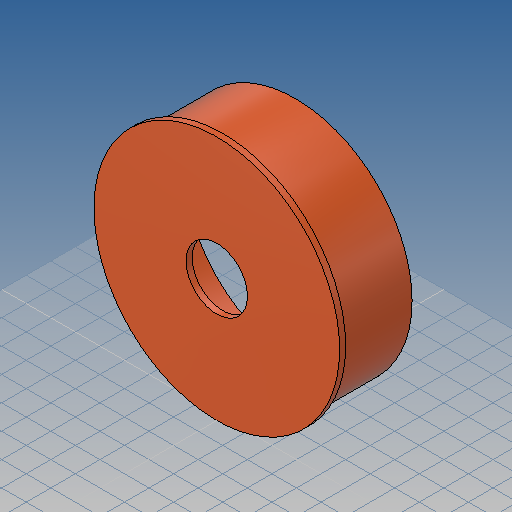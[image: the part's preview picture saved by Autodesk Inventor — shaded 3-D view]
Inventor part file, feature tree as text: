
AUTODESK INVENTOR PART (.ipt)
format: ipt  version: 2019 (Build 230136000, 136)  size: 133,632 bytes
history: native  units: mm
features: extrude x2, other x1, sketch x1
ambient origin geometry x8: Origin, YZ Plane, XZ Plane, XY Plane, X Axis, Y Axis, Z Axis, Center Point
bodies: Volumenkörper1 (feature_tree)
feature tree (4):
  other  "<userpath>\OneDrive\Dokumente\Inventor\Absauganlage\Absauganlage_Params.xlsx"
  sketch  "Skizze1"  dims[d0=200.0mm d1=4.9mm d2=5.5mm d3=4.9mm d4=0.0mm d5=59.0mm d6=0.0mm d7=50.0mm]
  extrude  "Extrusion1"  Depth=4.9mm
  extrude  "Extrusion2"  Depth=59.0mm
